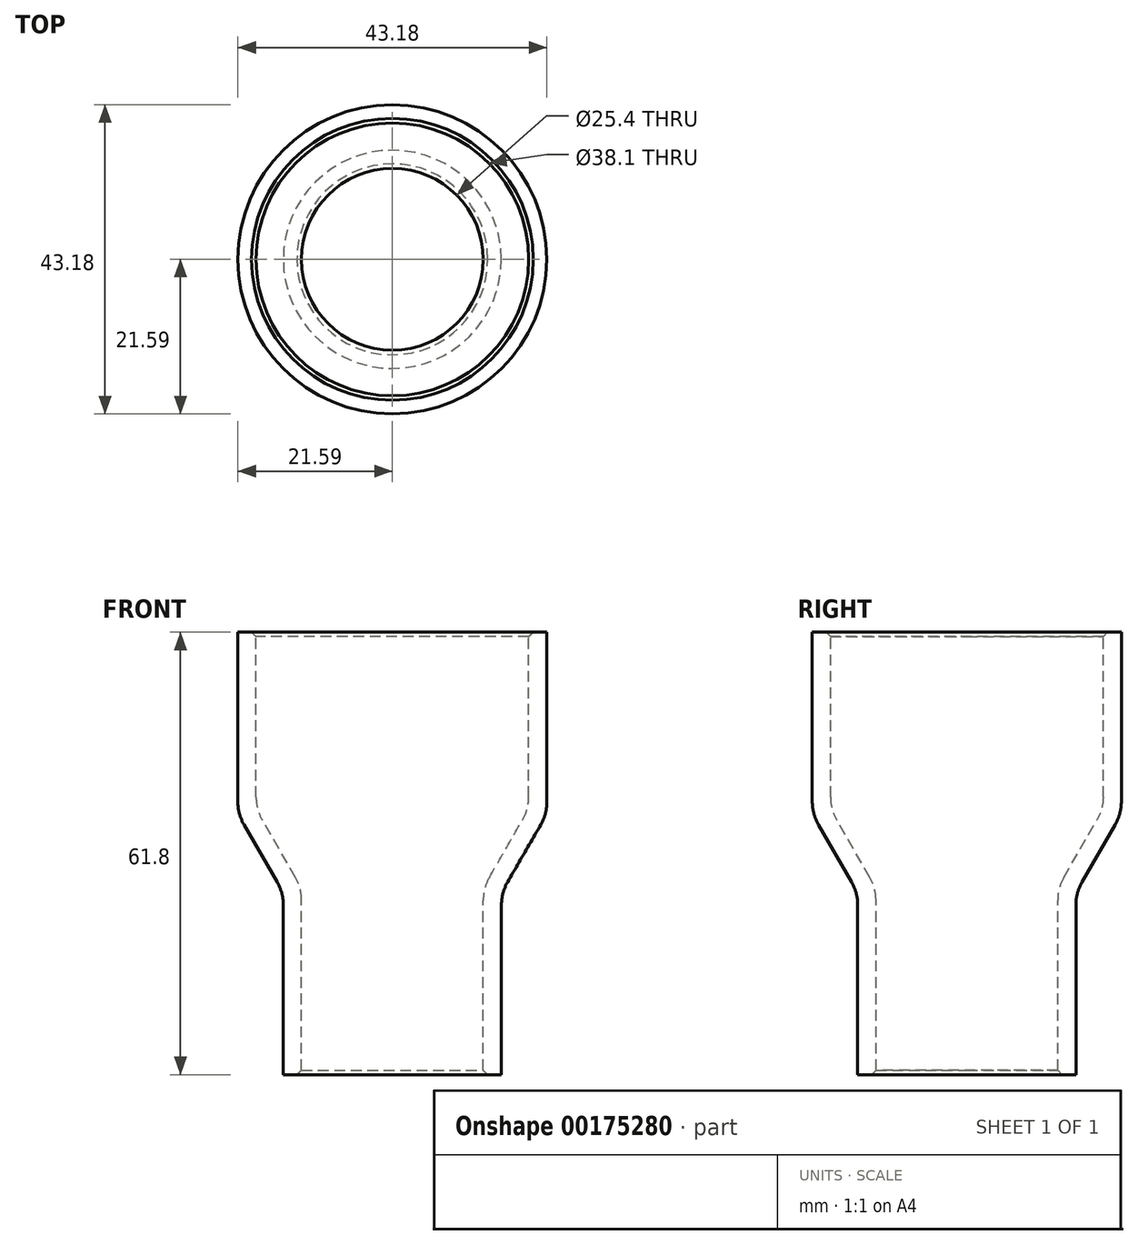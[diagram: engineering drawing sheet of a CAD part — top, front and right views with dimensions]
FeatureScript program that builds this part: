
annotation { "Feature Type Name" : "Feature", "Feature Type Description" : "" }
export const myFeature = defineFeature(function(context is Context, id is Id, definition is map)
    precondition{}
    {
        {
            var Q0;
            Q0=qCreatedBy(makeId("Front.planeOp"),FACE);
            var sketch = newSketch(context, id + "F0", { "sketchPlane" : qUnion([Q0])});
            skLineSegment(sketch, "E0", {"start": v(-21.59, 61.8) * mm, "end": v(-21.6, 36.4) * mm});
            skLineSegment(sketch, "E1", {"start": v(-21.6, 36.4) * mm, "end": v(-15.24, 25.4) * mm});
            skLineSegment(sketch, "E2", {"start": v(-15.24, 25.4) * mm, "end": v(-15.24, 0) * mm});
            skLineSegment(sketch, "E3", {"start": v(-15.24, 0) * mm, "end": v(-12.7, 0) * mm});
            skLineSegment(sketch, "E4", {"start": v(-12.7, 0) * mm, "end": v(-12.7, 26.08) * mm});
            skLineSegment(sketch, "E5", {"start": v(-12.7, 26.08) * mm, "end": v(-19.05, 37.08) * mm});
            skLineSegment(sketch, "E6", {"start": v(-19.05, 37.08) * mm, "end": v(-19.05, 61.8) * mm});
            skLineSegment(sketch, "E7", {"start": v(-19.05, 61.8) * mm, "end": v(-21.6, 61.8) * mm});
            skLineSegment(sketch, "E8", {"start": v(0, 61.8) * mm, "end": v(0, 0) * mm, "construction": true});
            skSolve(sketch);
        }
        {
            var Q0;
            Q0=makeQuery(id+"F0.imprint","IMPRINT",FACE,{"disambiguationData":[TD([[makeQuery(id+"F0.imprint","IMPRINT",EDGE,{"derivedFrom":sQuery(id+"F0.wireOp",EDGE,"E0")}),1.0]])]});
            var Q1;
            Q1=sQuery(id+"F0.wireOp",EDGE,"E8");
            var Q2;
            Q2=sQuery(id+"F0.wireOp",EDGE,"E8");
            revolve(context, id + "F1", {"entities" : qUnion([Q0]), "surfaceEntities" : qUnion([Q1]), "axis" : qUnion([Q2]), "revolveType" : RevolveType.FULL});
        }
        {
            var Q0;
            Q0=makeQuery(id+"F1.opRevolve","SWEPT_EDGE",EDGE,{"disambiguationData":[OSD([sQuery(id+"F0.wireOp",EDGE,"E0"),sQuery(id+"F0.wireOp",EDGE,"E1")])]});
            var Q1;
            Q1=makeQuery(id+"F1.opRevolve","SWEPT_EDGE",EDGE,{"disambiguationData":[OSD([sQuery(id+"F0.wireOp",EDGE,"E1"),sQuery(id+"F0.wireOp",EDGE,"E2")])]});
            var Q2;
            Q2=makeQuery(id+"F1.opRevolve","SWEPT_EDGE",EDGE,{"disambiguationData":[OSD([sQuery(id+"F0.wireOp",EDGE,"E5"),sQuery(id+"F0.wireOp",EDGE,"E6")])]});
            var Q3;
            Q3=makeQuery(id+"F1.opRevolve","SWEPT_EDGE",EDGE,{"disambiguationData":[OSD([sQuery(id+"F0.wireOp",EDGE,"E4"),sQuery(id+"F0.wireOp",EDGE,"E5")])]});
            fillet(context, id + "F2", {"entities" : qUnion([Q0, Q1, Q2, Q3]), "radius" : 6.35 * mm, "tangentPropagation" : true, "allowEdgeOverflow" : false});
        }
        {
            var Q0;
            Q0=makeQuery(id+"F1.opRevolve","SWEPT_EDGE",EDGE,{"disambiguationData":[OSD([sQuery(id+"F0.wireOp",EDGE,"E3"),sQuery(id+"F0.wireOp",EDGE,"E4")])]});
            var Q1;
            Q1=makeQuery(id+"F1.opRevolve","SWEPT_EDGE",EDGE,{"disambiguationData":[OSD([sQuery(id+"F0.wireOp",EDGE,"E6"),sQuery(id+"F0.wireOp",EDGE,"E7")])]});
            chamfer(context, id + "F3", {"entities" : qUnion([Q0, Q1]), "width" : 0.64 * mm, "tangentPropagation" : true});
        }
    });
